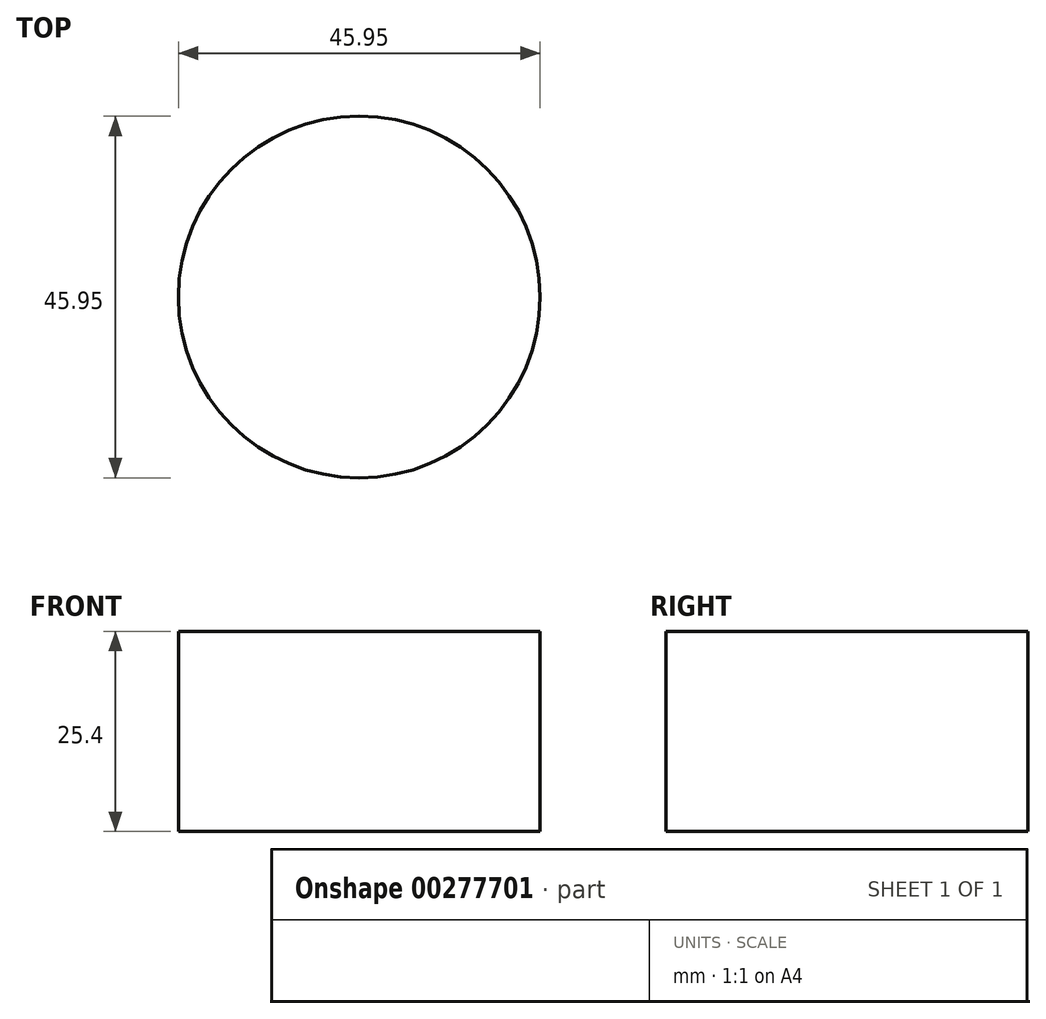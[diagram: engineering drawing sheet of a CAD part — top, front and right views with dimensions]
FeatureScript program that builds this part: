
annotation { "Feature Type Name" : "Feature", "Feature Type Description" : "" }
export const myFeature = defineFeature(function(context is Context, id is Id, definition is map)
    precondition{}
    {
        {
            var Q0;
            Q0=qCreatedBy(makeId("Top.planeOp"),FACE);
            var sketch = newSketch(context, id + "F0", { "sketchPlane" : qUnion([Q0])});
            skArc(sketch, "E0", {"start": v(0, 0) * mm, "mid": v(26.62, 35.17) * mm, "end": v(-16.03, 23.92) * mm});
            skArc(sketch, "E1", {"start": v(-24.7, 23.92) * mm, "mid": v(-20.36, -8.81) * mm, "end": v(-16.03, 23.92) * mm});
            skArc(sketch, "E2", {"start": v(0, -15.54) * mm, "mid": v(14, 14.94) * mm, "end": v(-16.03, 0) * mm});
            skCircle(sketch, "E3", {"center": v(-44.03, -16.11) * mm, "radius": 22.98 * mm});
            skFitSpline(sketch, "E4", {"points": [v(-24.7, 23.92) * mm, v(-31.99, 47.3) * mm, v(-24.7, 56.96) * mm, v(-8.9, 48.84) * mm, v(-4.01, 30.37) * mm, v(-11.89, 22.18) * mm, v(-16.03, 22.18) * mm, v(-24.7, 23.92) * mm]});
            skSolve(sketch);
        }
        {
            var Q0;
            Q0=sQuery(id+"F0.wireOp",EDGE,"E3");
            extrude(context, id + "F1", {"bodyType" : ToolBodyType.SURFACE, "surfaceEntities" : qUnion([Q0]), "depth" : 25.4 * mm});
        }
    });
